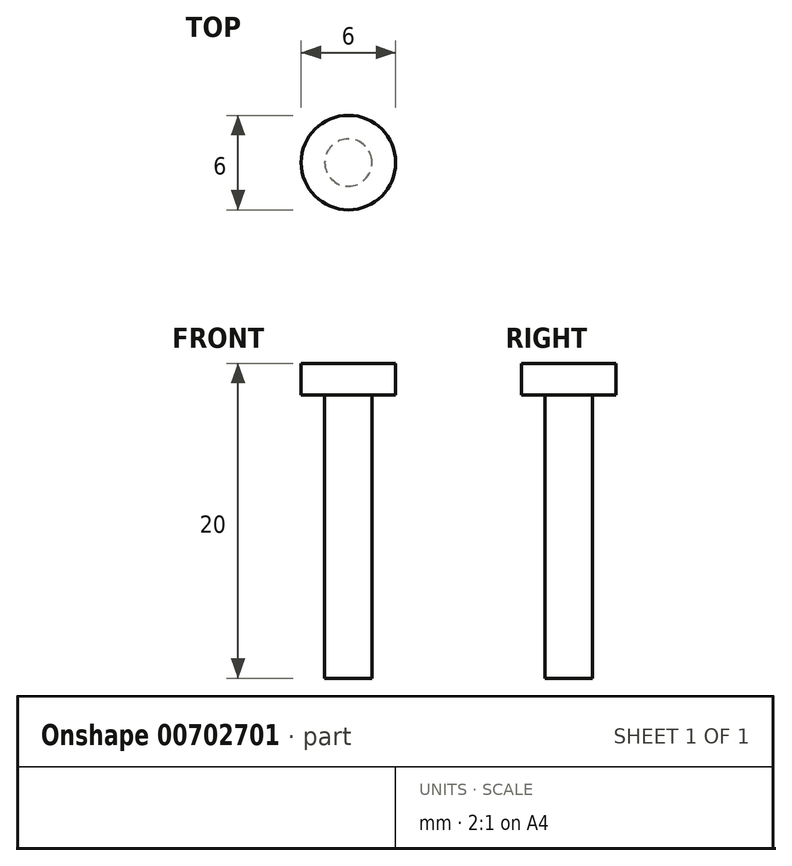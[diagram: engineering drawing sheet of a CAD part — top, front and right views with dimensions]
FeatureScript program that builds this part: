
annotation { "Feature Type Name" : "Feature", "Feature Type Description" : "" }
export const myFeature = defineFeature(function(context is Context, id is Id, definition is map)
    precondition{}
    {
        {
            var Q0;
            Q0=qCreatedBy(makeId("Front.planeOp"),FACE);
            var sketch = newSketch(context, id + "F0", { "sketchPlane" : qUnion([Q0])});
            skLineSegment(sketch, "E0", {"start": v(-1.5, 12.67) * mm, "end": v(1.5, 12.67) * mm});
            skLineSegment(sketch, "E1", {"start": v(1.5, 12.67) * mm, "end": v(1.5, 10.67) * mm});
            skLineSegment(sketch, "E2", {"start": v(1.5, 10.67) * mm, "end": v(0, 10.67) * mm});
            skLineSegment(sketch, "E3", {"start": v(0, 10.67) * mm, "end": v(0, -7.33) * mm});
            skLineSegment(sketch, "E4", {"start": v(0, -7.33) * mm, "end": v(-1.5, -7.33) * mm});
            skLineSegment(sketch, "E5", {"start": v(-1.5, -7.33) * mm, "end": v(-1.5, 12.67) * mm});
            skSolve(sketch);
        }
        {
            var Q0;
            Q0=makeQuery(id+"F0.imprint","IMPRINT",FACE,{"disambiguationData":[TD([[makeQuery(id+"F0.imprint","IMPRINT",EDGE,{"derivedFrom":sQuery(id+"F0.wireOp",EDGE,"E0")}),-1.0]])]});
            var Q1;
            Q1=sQuery(id+"F0.wireOp",EDGE,"E5");
            revolve(context, id + "F1", {"surfaceOperationType" : NewSurfaceOperationType.NEW, "entities" : qUnion([Q0]), "axis" : qUnion([Q1]), "revolveType" : RevolveType.FULL});
        }
    });
